# Revit family: Urimat - Compactplus
name_source: partatom
category: Plumbing Fixtures
revit_build: Autodesk Revit 2018 (Build: 20181015_0930(x64)
units: mm (PartAtom-declared; Revit-internal decimal feet)

## family parameters
Always vertical = Yes
Cut with Voids When Loaded = No
OmniClass Number = 23.45.05.21.11.21
OmniClass Title = Urinals
Part Type = Normal
Room Calculation Point = No
Round Connector Dimension = Use Diameter
Shared = No
Work Plane-Based = No

## types (1)
- Urimat - Compactplus
    CW Connection = Yes
    Code = 14001
    Cold water connection Diameter = 15 mm
    Cold water connection Flowrate = 0.0 L/s
    Color = white
    Depth = 340 mm
    HW Connection = No
    Height = 720 mm  [stored 2.3622 ft]
    Manufacturer = Urimat
    Material = <By Category>
    Material 2 = <By Category>
    Material type = polycarbonate
    Product line subcategory = Compact
    R1 = 365 mm  [stored 1.19751 ft]
    R2 = 720 mm  [stored 2.3622 ft]
    R3 = 340 mm
    R4 = 15 mm  [stored 0.0492126 ft]
    R5 = 50 mm  [stored 0.164042 ft]
    Vent Connection = No
    W1 = No
    Waste Connection = Yes
    Waste Connection Flowrate = 0.0 L/s
    Waste connection Diameter = 50 mm
    Weight = 3.50 kg
    Width = 365 mm  [stored 1.19751 ft]
    With display = No

note: [stored X ft] marks values corroborated as IEEE doubles in the binary element streams (Revit-internal decimal feet)

## geometry (parser evidence)
native form markers: Blend x2, Sweep x5
no freeform markers — native parametric forms only
